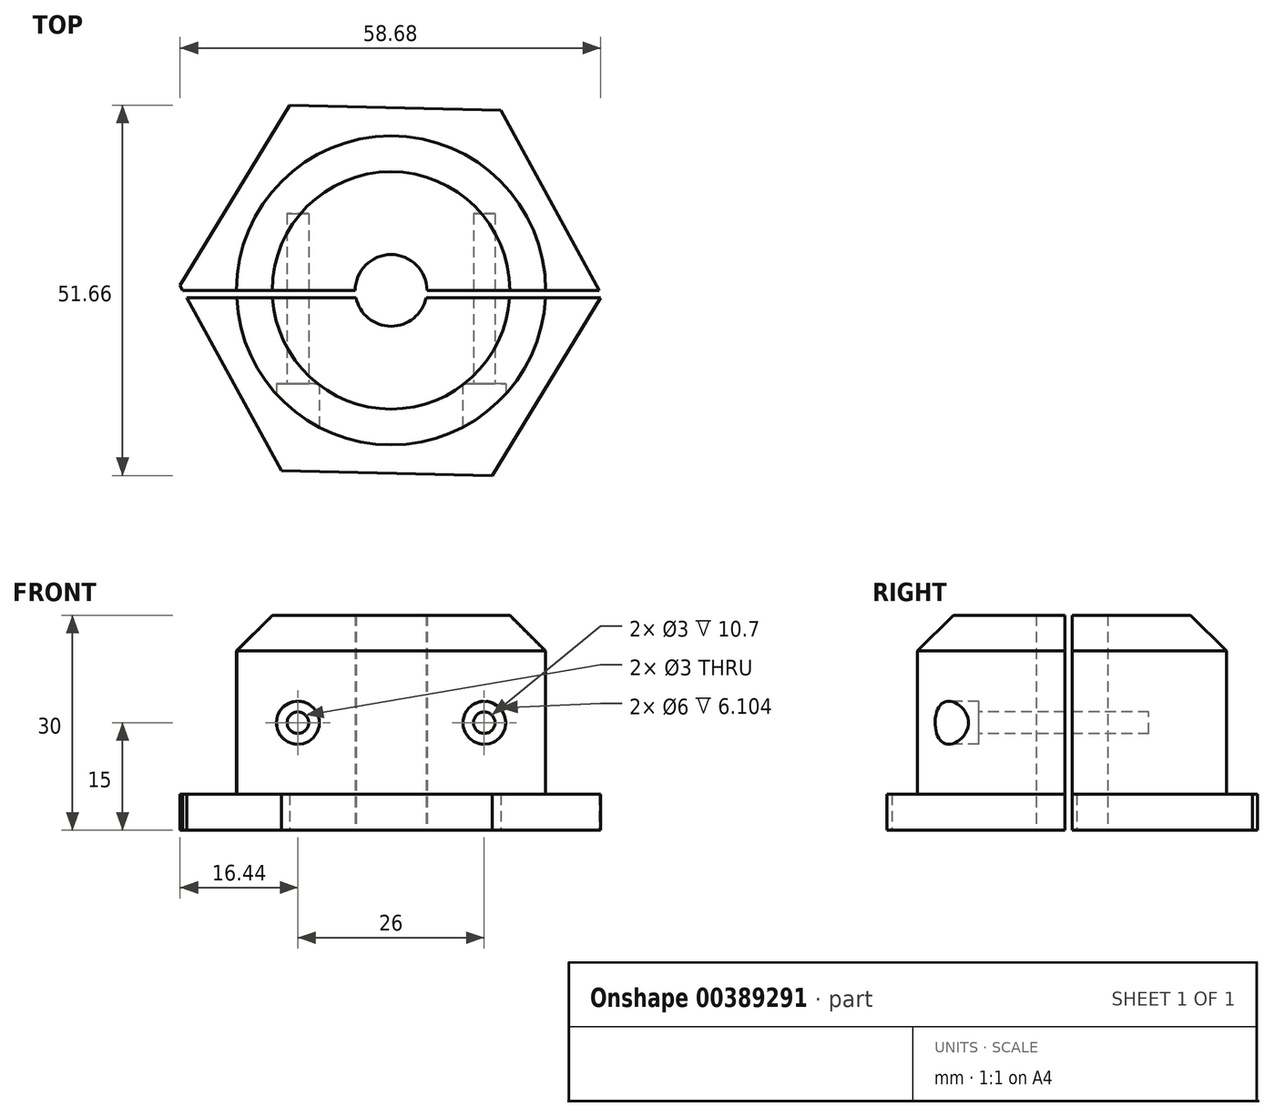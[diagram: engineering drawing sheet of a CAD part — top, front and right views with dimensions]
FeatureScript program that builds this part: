
annotation { "Feature Type Name" : "Feature", "Feature Type Description" : "" }
export const myFeature = defineFeature(function(context is Context, id is Id, definition is map)
    precondition{}
    {
        {
            var Q0;
            Q0=qCreatedBy(makeId("Top.planeOp"),FACE);
            var sketch = newSketch(context, id + "F0", { "sketchPlane" : qUnion([Q0])});
            skCircle(sketch, "E0.cCircle", {"center": v(0, 0) * mm, "radius": 25.5 * mm, "construction": true});
            skLineSegment(sketch, "E0.0", {"start": v(-29.44, 0.68) * mm, "end": v(-14.13, 25.83) * mm});
            skLineSegment(sketch, "E0.1", {"start": v(-14.13, 25.83) * mm, "end": v(15.3, 25.15) * mm});
            skLineSegment(sketch, "E0.2", {"start": v(15.3, 25.15) * mm, "end": v(29.44, -0.68) * mm});
            skLineSegment(sketch, "E0.3", {"start": v(29.44, -0.68) * mm, "end": v(14.13, -25.83) * mm});
            skLineSegment(sketch, "E0.4", {"start": v(14.13, -25.83) * mm, "end": v(-15.3, -25.15) * mm});
            skLineSegment(sketch, "E0.5", {"start": v(-15.3, -25.15) * mm, "end": v(-29.44, 0.68) * mm});
            skPoint(sketch, "E0.0.midPoint", {"position": v(-21.78, 13.26) * mm});
            skCircle(sketch, "E1", {"center": v(0, 0) * mm, "radius": 5 * mm});
            skSolve(sketch);
        }
        {
            var Q0;
            Q0 = qSketchRegion(id + "F0", true);
            extrude(context, id + "F1", {"entities" : qUnion([Q0]), "depth" : 5 * mm, "offsetDistance" : 25 * mm});
        }
        {
            var Q0;
            Q0=makeQuery(id+"F1.opExtrude","CAP_FACE",FACE,{"disambiguationData":[OSD([sQuery(id+"F0.wireOp",EDGE,"E0.0"),sQuery(id+"F0.wireOp",EDGE,"E0.1"),sQuery(id+"F0.wireOp",EDGE,"E0.2"),sQuery(id+"F0.wireOp",EDGE,"E0.3"),sQuery(id+"F0.wireOp",EDGE,"E0.4"),sQuery(id+"F0.wireOp",EDGE,"E0.5"),sQuery(id+"F0.wireOp",EDGE,"E1")])],"isStart":false});
            var sketch = newSketch(context, id + "F2", { "sketchPlane" : qUnion([Q0])});
            skCircle(sketch, "E2", {"center": v(0, 0) * mm, "radius": 21.56 * mm});
            skSolve(sketch);
        }
        {
            var Q0;
            Q0 = qSketchRegion(id + "F2", true);
            extrude(context, id + "F3", {"entities" : qUnion([Q0]), "operationType" : NewBodyOperationType.ADD, "depth" : 25 * mm, "offsetDistance" : 25 * mm});
        }
        {
            var Q0;
            Q0=makeQuery(id+"F3.opExtrude","CAP_EDGE",EDGE,{"disambiguationData":[OSD([sQuery(id+"F2.wireOp",EDGE,"E2")])],"isStart":false});
            chamfer(context, id + "F4", {"entities" : qUnion([Q0]), "width" : 5 * mm, "tangentPropagation" : true});
        }
        {
            var Q0;
            Q0=makeQuery(id+"F3.opExtrude","CAP_FACE",FACE,{"disambiguationData":[OSD([sQuery(id+"F2.wireOp",EDGE,"E2")])],"isStart":true});
            extrude(context, id + "F5", {"entities" : qUnion([Q0]), "operationType" : NewBodyOperationType.REMOVE, "endBound" : BoundingType.THROUGH_ALL, "oppositeDirection" : true, "depth" : 25 * mm, "offsetDistance" : 25 * mm});
        }
        {
            var Q0;
            Q0=qCreatedBy(makeId("Front.planeOp"),FACE);
            cPlane(context, id + "F6", {"entities" : qUnion([Q0]), "cplaneType" : CPlaneType.OFFSET, "offset" : 20 * mm, "width" : 150 * mm, "height" : 150 * mm});
        }
        {
            var Q0;
            Q0=qCreatedBy(id+"F6.planeOp",FACE);
            var sketch = newSketch(context, id + "F7", { "sketchPlane" : qUnion([Q0])});
            skCircle(sketch, "E3", {"center": v(-13, 15) * mm, "radius": 1.5 * mm});
            skCircle(sketch, "E4", {"center": v(13, 15) * mm, "radius": 1.5 * mm});
            skCircle(sketch, "E5", {"center": v(-13, 15) * mm, "radius": 3 * mm});
            skCircle(sketch, "E6", {"center": v(13, 15) * mm, "radius": 3 * mm});
            skSolve(sketch);
        }
        {
            var Q0;
            Q0=makeQuery(id+"F7.imprint","IMPRINT",FACE,{"disambiguationData":[TD([[makeQuery(id+"F7.imprint","IMPRINT",EDGE,{"derivedFrom":sQuery(id+"F7.wireOp",EDGE,"E4")}),1.0]])]});
            var Q1;
            Q1=makeQuery(id+"F7.imprint","IMPRINT",FACE,{"disambiguationData":[TD([[makeQuery(id+"F7.imprint","IMPRINT",EDGE,{"derivedFrom":sQuery(id+"F7.wireOp",EDGE,"E4")}),-1.0]])]});
            var Q2;
            Q2=makeQuery(id+"F7.imprint","IMPRINT",FACE,{"disambiguationData":[TD([[makeQuery(id+"F7.imprint","IMPRINT",EDGE,{"derivedFrom":sQuery(id+"F7.wireOp",EDGE,"E3")}),-1.0]])]});
            var Q3;
            Q3=makeQuery(id+"F7.imprint","IMPRINT",FACE,{"disambiguationData":[TD([[makeQuery(id+"F7.imprint","IMPRINT",EDGE,{"derivedFrom":sQuery(id+"F7.wireOp",EDGE,"E3")}),1.0]])]});
            extrude(context, id + "F8", {"entities" : qUnion([Q0, Q1, Q2, Q3]), "operationType" : NewBodyOperationType.REMOVE, "oppositeDirection" : true, "depth" : 7 * mm, "offsetDistance" : 25 * mm});
        }
        {
            var Q0;
            Q0=makeQuery(id+"F7.imprint","IMPRINT",FACE,{"disambiguationData":[TD([[makeQuery(id+"F7.imprint","IMPRINT",EDGE,{"derivedFrom":sQuery(id+"F7.wireOp",EDGE,"E3")}),1.0]])]});
            var Q1;
            Q1=makeQuery(id+"F7.imprint","IMPRINT",FACE,{"disambiguationData":[TD([[makeQuery(id+"F7.imprint","IMPRINT",EDGE,{"derivedFrom":sQuery(id+"F7.wireOp",EDGE,"E4")}),1.0]])]});
            extrude(context, id + "F9", {"entities" : qUnion([Q0, Q1]), "operationType" : NewBodyOperationType.REMOVE, "oppositeDirection" : true, "depth" : 30.7 * mm, "offsetDistance" : 25 * mm});
        }
        {
            var Q0;
            Q0=qCreatedBy(makeId("Right.planeOp"),FACE);
            var sketch = newSketch(context, id + "F10", { "sketchPlane" : qUnion([Q0])});
            skLineSegment(sketch, "E7.bottom", {"start": v(0, 37.87) * mm, "end": v(-1, 37.87) * mm});
            skLineSegment(sketch, "E7.top", {"start": v(0, -2.13) * mm, "end": v(-1, -2.13) * mm});
            skLineSegment(sketch, "E7.left", {"start": v(0, 37.87) * mm, "end": v(0, -2.13) * mm});
            skLineSegment(sketch, "E7.right", {"start": v(-1, 37.87) * mm, "end": v(-1, -2.13) * mm});
            skSolve(sketch);
        }
        {
            var Q0;
            Q0 = qSketchRegion(id + "F10", true);
            extrude(context, id + "F11", {"entities" : qUnion([Q0]), "operationType" : NewBodyOperationType.REMOVE, "oppositeDirection" : true, "depth" : 100 * mm, "offsetDistance" : 25 * mm, "symmetric" : true});
        }
    });
